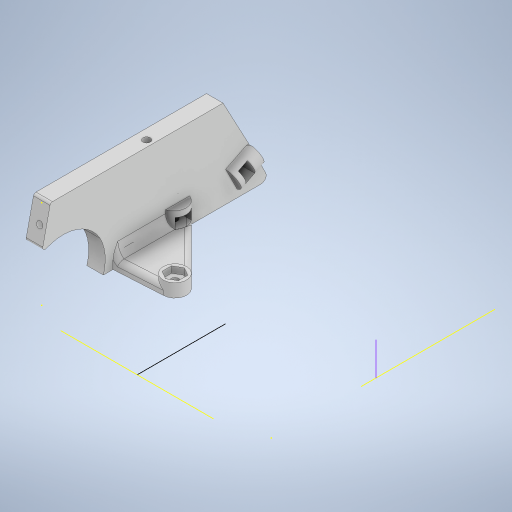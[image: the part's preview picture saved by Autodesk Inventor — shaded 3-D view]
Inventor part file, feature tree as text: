
AUTODESK INVENTOR PART (.ipt)
format: ipt  version: 2023 (Build 270158000, 158)  size: 3,066,368 bytes
history: native  units: mm
features: projected_geometry x135, extrude x121, sketch x89, fillet x11, reference x5, plane x3, mirror x3, other x3
ambient origin geometry x8: Origin, YZ Plane, XZ Plane, XY Plane, X Axis, Y Axis, Z Axis, Center Point
bodies: Solid1 (feature_tree)
feature tree (370):
  sketch  "Sketch1"  dims[d0=100.0mm d1=100.0mm]
  extrude  "Extrusion1"  Depth=100.0mm
  extrude  "Extrusion2"  Depth=20.0mm
  extrude  "Extrusion3"  Depth=20.0mm
  sketch  "Sketch3"  dims[d4=31.0mm d5=20.0mm]
  extrude  "Extrusion4"  Depth=19.0mm
  extrude  "Extrusion5"  Depth=10.0mm
  sketch  "Sketch4"  dims[d6=14.0mm d7=19.0mm]
  plane  "Work Plane1"
  mirror  "Mirror1"
  extrude  "Extrusion6"  Depth=10.0mm
  sketch  "Sketch8"  dims[d10=10.0mm d11=2.0mm]
  extrude  "Extrusion7"  Depth=15.0mm
  extrude  "Extrusion8"  Depth=2.0mm
  extrude  "Extrusion9"  Depth=1.0mm
  sketch  "Sketch9"  dims[d12=2.0mm d13=15.0mm]
  extrude  "Extrusion10"  Depth=10.0mm TaperAngle=0.0deg
  extrude  "Extrusion11"  TaperAngle=0.0deg  [1 undecoded]
  sketch  "Sketch10"  dims[d14=15.0mm d15=2.0mm]
  extrude  "Extrusion12"  Depth=14.0mm TaperAngle=0.0deg
  extrude  "Extrusion13"  TaperAngle=90.0deg  [1 undecoded]
  extrude  "Extrusion14"  Depth=40.0mm
  sketch  "Sketch12"  dims[d18=10.0mm d19=0.0mm d20=2.0mm d21=0.0mm]
  extrude  "Extrusion15"  Depth=25.0mm
  extrude  "Extrusion16"  Depth=5.0mm
  extrude  "Extrusion17"  Depth=13.0mm
  extrude  "Extrusion18"  Depth=8.0mm
  extrude  "Extrusion19"  Depth=18.0mm TaperAngle=0.0deg
  extrude  "Extrusion20"  Depth=49.0mm
  extrude  "Extrusion21"  Depth=5.0mm
  sketch  "Sketch15"  dims[d28=14.25mm d29=0.0mm d30=90.0deg]
  plane  "Work Plane2"
  mirror  "Mirror2"
  extrude  "Extrusion22"  TaperAngle=0.0deg  [1 undecoded]
  sketch  "Sketch17"  dims[d36=15.0mm d37=25.0mm]
  extrude  "Extrusion23"  Depth=10.0mm
  extrude  "Extrusion24"  Depth=1.6mm
  extrude  "Extrusion25"  TaperAngle=0.0deg  [1 undecoded]
  extrude  "Extrusion26"  Depth=14.0mm TaperAngle=0.0deg
  extrude  "Extrusion27"  Depth=6.0mm
  sketch  "Sketch21"  dims[d44=18.0mm d45=0.0mm d46=18.0mm d47=0.0mm]
  extrude  "Extrusion28"  Depth=2.0mm
  extrude  "Extrusion29"  Depth=6.0mm TaperAngle=0.0deg
  sketch  "Sketch22"  dims[d48=0.0mm d49=0.0mm d50=49.0mm]
  extrude  "Extrusion30"  Depth=15.0mm TaperAngle=0.0deg
  extrude  "Extrusion31"  Depth=3.2mm
  extrude  "Extrusion32"  Depth=4.0mm
  extrude  "Extrusion33"  Depth=1.0mm TaperAngle=0.0deg
  extrude  "Extrusion34"  Depth=3.0mm
  extrude  "Extrusion35"  Depth=15.0mm TaperAngle=0.0deg
  extrude  "Extrusion36"  Depth=3.2mm
  fillet  "Face Fillet1"
  fillet  "Face Fillet2"
  extrude  "Extrusion37"  Depth=3.2mm
  fillet  "Face Fillet3"
  fillet  "Face Fillet5"
  extrude  "Extrusion38"  Depth=5.0mm TaperAngle=0.0deg
  extrude  "Extrusion39"  TaperAngle=0.0deg  [1 undecoded]
  fillet  "Fillet2"  Radius=2.8mm
  extrude  "Extrusion40"  Depth=100.0mm TaperAngle=0.0deg
  sketch  "Sketch32"  dims[d76=6.0mm d77=0.0mm d78=15.0mm d79=0.0mm]
  extrude  "Extrusion41"  Depth=11.0mm
  extrude  "Extrusion42"  Depth=9.0mm TaperAngle=0.0deg
  extrude  "Extrusion43"  Depth=3.2mm
  sketch  "Sketch33"  dims[d80=15.0mm d81=0.0mm d82=3.2mm]
  extrude  "Extrusion44"  Depth=7.0mm TaperAngle=0.0deg
  extrude  "Extrusion45"  Depth=40.656mm TaperAngle=0.0deg
  extrude  "Extrusion46"  Depth=9.0mm TaperAngle=0.0deg
  extrude  "Extrusion47"  Depth=3.0mm
  sketch  "Sketch36"  dims[d91=90.0deg d92=3.0mm]
  extrude  "Extrusion48"  Depth=1.5mm TaperAngle=0.0deg
  extrude  "Extrusion49"  Depth=6.0mm
  sketch  "Sketch37"  dims[d93=3.0mm d94=15.0mm d95=0.0mm]
  extrude  "Extrusion50"  Depth=10.0mm TaperAngle=0.0deg
  extrude  "Extrusion51"  Depth=4.0mm
  extrude  "Extrusion52"  Depth=10.0mm TaperAngle=0.0deg
  extrude  "Extrusion53"  Depth=20.0mm TaperAngle=0.0deg
  sketch  "Sketch40"  dims[d100=4.0mm d101=5.0mm d102=0.0mm]
  extrude  "Extrusion54"  Depth=1.5mm
  extrude  "Extrusion55"  Depth=3.0mm
  extrude  "Extrusion56"  Depth=6.4mm
  extrude  "Extrusion57"  Depth=3.0mm
  fillet  "Fillet3"  Radius=2.0mm
  extrude  "Extrusion58"  TaperAngle=0.0deg  [1 undecoded]
  sketch  "Sketch44"  dims[d114=3.4mm d115=9.0mm d116=0.0mm]
  extrude  "Extrusion59"  TaperAngle=0.0deg  [1 undecoded]
  extrude  "Extrusion60"  Depth=10.0mm TaperAngle=0.0deg
  sketch  "Sketch45"  dims[d117=15.0mm d118=0.0mm d119=3.2mm]
  extrude  "Extrusion61"  Depth=10.0mm TaperAngle=0.0deg
  extrude  "Extrusion62"  Depth=3.0mm
  sketch  "Sketch46"  dims[d120=3.2mm d121=7.0mm d122=0.0mm]
  extrude  "Extrusion63"  Depth=6.5mm TaperAngle=0.0deg
  extrude  "Extrusion64"  Depth=17.0mm TaperAngle=0.0deg
  extrude  "Extrusion65"  Depth=3.0mm
  extrude  "Extrusion66"  Depth=5.0mm TaperAngle=0.0deg
  sketch  "Sketch49"  dims[d138=28.734mm d139=3.0mm]
  extrude  "Extrusion67"  Depth=6.5mm TaperAngle=0.0deg
  extrude  "Extrusion68"  Depth=14.0mm TaperAngle=0.0deg
  extrude  "Extrusion69"  Depth=6.5mm
  extrude  "Extrusion70"  Depth=6.5mm TaperAngle=0.0deg
  extrude  "Extrusion71"  Depth=17.0mm TaperAngle=0.0deg
  extrude  "Extrusion72"  Depth=2.5mm
  extrude  "Extrusion73"  Depth=2.0mm
  extrude  "Extrusion74"  TaperAngle=0.0deg  [1 undecoded]
  extrude  "Extrusion75"  Depth=6.5mm TaperAngle=0.0deg
  extrude  "Extrusion76"  Depth=1.0mm
  sketch  "Sketch53"  dims[d149=6.7mm d152=4.0mm]
  extrude  "Extrusion77"  Depth=1.0mm
  extrude  "Extrusion78"  Depth=3.0mm
  extrude  "Extrusion79"  Depth=15.0mm TaperAngle=0.0deg
  extrude  "Extrusion80"  Depth=10.0mm TaperAngle=0.0deg
  extrude  "Extrusion81"  Depth=10.0mm TaperAngle=0.0deg
  extrude  "Extrusion82"  Depth=4.0mm TaperAngle=0.0deg
  extrude  "Extrusion83"  Depth=10.0mm TaperAngle=0.0deg
  sketch  "Sketch59"  dims[d166=6.4mm d167=3.0mm d169=2.0mm]
  extrude  "Extrusion84"  Depth=7.0mm
  extrude  "Extrusion85"  Depth=6.5mm TaperAngle=0.0deg
  extrude  "Extrusion86"  Depth=4.0mm TaperAngle=0.0deg
  extrude  "Extrusion87"  Depth=1.0mm
  extrude  "Extrusion88"  Depth=10.0mm TaperAngle=0.0deg
  sketch  "Sketch62"  dims[d178=10.0mm d179=0.0mm d180=4.0mm d181=0.0mm]
  extrude  "Extrusion89"  Depth=10.0mm
  extrude  "Extrusion90"  Depth=10.0mm
  fillet  "Fillet4"  Radius=30.0mm
  extrude  "Extrusion91"  Depth=10.0mm
  extrude  "Extrusion92"  Depth=10.0mm
  extrude  "Extrusion93"  Depth=10.0mm TaperAngle=0.0deg
  extrude  "Extrusion94"  TaperAngle=135.0deg  [1 undecoded]
  extrude  "Extrusion95"  TaperAngle=0.0deg  [1 undecoded]
  sketch  "Sketch68"  dims[d205=4.0mm d206=0.0mm d207=5.0mm d208=0.0mm]
  extrude  "Extrusion96"  Depth=10.0mm TaperAngle=0.0deg
  extrude  "Extrusion97"  Depth=10.0mm
  extrude  "Extrusion98"  Depth=10.0mm
  extrude  "Extrusion99"  Depth=10.0mm
  extrude  "Extrusion100"  TaperAngle=0.0deg  [1 undecoded]
  sketch  "Sketch74"  dims[d219=6.5mm d220=0.0mm d221=16.0mm d222=0.0mm]
  extrude  "Extrusion101"  Depth=1.0mm TaperAngle=0.0deg
  extrude  "Extrusion102"  Depth=10.0mm TaperAngle=0.0deg
  extrude  "Extrusion103"  Depth=10.0mm TaperAngle=0.0deg
  extrude  "Extrusion104"  Depth=10.0mm TaperAngle=0.0deg
  extrude  "Extrusion105"  Depth=10.0mm TaperAngle=0.0deg
  fillet  "Fillet6"  Radius=12.0mm
  fillet  "Fillet7"  Radius=2.0mm
  extrude  "Extrusion106"  Depth=10.0mm TaperAngle=0.0deg
  fillet  "Fillet8"  Radius=5.0mm
  extrude  "Extrusion107"  Depth=6.5mm TaperAngle=0.0deg
  sketch  "Sketch80"  dims[d239=1.0mm d240=2.5mm]
  extrude  "Extrusion108"  Depth=10.0mm
  extrude  "Extrusion109"  Depth=10.0mm TaperAngle=0.0deg
  extrude  "Extrusion110"  Depth=10.0mm TaperAngle=0.0deg
  extrude  "Extrusion111"  Depth=10.0mm
  extrude  "Extrusion112"  Depth=10.0mm
  fillet  "Fillet9"  Radius=3.5mm
  extrude  "Extrusion113"  Depth=10.0mm
  extrude  "Extrusion114"  Depth=6.5mm TaperAngle=0.0deg
  extrude  "Extrusion115"  Depth=6.5mm TaperAngle=0.0deg
  plane  "Work Plane3"
  mirror  "Mirror3"
  extrude  "Extrusion116"  Depth=10.0mm
  extrude  "Extrusion117"  Depth=10.0mm TaperAngle=0.0deg
  sketch  "Sketch89"  dims[d269=6.5mm d270=0.0mm d271=3.0mm d272=0.0mm]
  extrude  "Extrusion118"  Depth=10.0mm TaperAngle=0.0deg
  extrude  "Extrusion119"  Depth=10.0mm
  extrude  "Wyciągnięcie proste120"  TaperAngle=90.0deg  [1 undecoded]
  extrude  "Wyciągnięcie proste121"  Depth=10.0mm
  sketch  "Sketch2"  dims[d2=5.0mm d3=20.0mm]
  projected_geometry  "Projected Loop1"
  sketch  "Sketch6"  dims[d8=10.0mm d9=14.0mm]
  projected_geometry  "Projected Loop5"
  projected_geometry  "Projected Loop6"
  projected_geometry  "Projected Loop7"
  projected_geometry  "Projected Loop8"
  projected_geometry  "Projected Loop9"
  projected_geometry  "Projected Loop10"
  sketch  "Sketch11"  dims[d16=1.0mm d17=5.0mm]
  projected_geometry  "Projected Loop11"
  projected_geometry  "Projected Loop12"
  sketch  "Sketch13"  dims[d22=31.0mm d23=0.0mm d24=0.0mm]
  projected_geometry  "Projected Loop13"
  projected_geometry  "Projected Loop14"
  sketch  "Sketch14"  dims[d25=30.4mm d26=14.0mm d27=0.0mm]
  projected_geometry  "Projected Loop15"
  projected_geometry  "Projected Loop16"
  sketch  "Sketch16"  dims[d33=25.0mm d34=0.0mm d35=40.0mm]
  projected_geometry  "Projected Loop17"
  projected_geometry  "Projected Loop18"
  projected_geometry  "Projected Loop19"
  sketch  "Sketch18"  dims[d38=20.0mm d39=5.0mm]
  projected_geometry  "Projected Loop20"
  projected_geometry  "Projected Loop21"
  projected_geometry  "Projected Loop22"
  projected_geometry  "Projected Loop23"
  projected_geometry  "Projected Loop24"
  projected_geometry  "Projected Loop25"
  projected_geometry  "Projected Loop26"
  sketch  "Sketch19"  dims[d40=7.0mm d41=13.0mm]
  projected_geometry  "Projected Loop27"
  sketch  "Sketch20"  dims[d42=7.0mm d43=8.0mm]
  projected_geometry  "Projected Loop28"
  projected_geometry  "Projected Loop29"
  projected_geometry  "Projected Loop30"
  sketch  "Sketch23"  dims[d51=25.0mm d52=5.0mm]
  sketch  "Sketch24"  dims[d53=20.0mm d54=0.0mm d55=0.0mm]
  projected_geometry  "Projected Loop31"
  projected_geometry  "Projected Loop32"
  sketch  "Sketch25"  dims[d56=10.0mm d57=0.0mm d58=1.6mm]
  projected_geometry  "Projected Loop33"
  sketch  "Sketch26"  dims[d59=1.6mm d60=1.6mm]
  projected_geometry  "Projected Loop34"
  sketch  "Sketch27"  dims[d61=5.0mm d62=0.0mm d63=0.0mm d64=0.0mm]
  projected_geometry  "Projected Loop35"
  sketch  "Sketch28"  dims[d65=2.5mm d66=14.0mm d67=0.0mm]
  projected_geometry  "Projected Loop36"
  sketch  "Sketch29"  dims[d68=2.0mm d69=6.0mm]
  sketch  "Sketch30"  dims[d70=5.0mm d71=2.0mm]
  projected_geometry  "Projected Loop37"
  projected_geometry  "Projected Loop38"
  projected_geometry  "Projected Loop39"
  sketch  "Sketch31"  dims[d72=14.0mm d73=0.0mm d74=6.0mm d75=0.0mm]
  projected_geometry  "Projected Loop40"
  projected_geometry  "Projected Loop41"
  projected_geometry  "Projected Loop42"
  projected_geometry  "Projected Loop43"
  projected_geometry  "Projected Loop44"
  projected_geometry  "Projected Loop45"
  projected_geometry  "Projected Loop46"
  sketch  "Sketch34"  dims[d83=3.2mm d84=4.0mm]
  projected_geometry  "Projected Loop47"
  projected_geometry  "Projected Loop48"
  sketch  "Sketch35"  dims[d85=15.0mm d86=0.0mm d87=1.0mm d88=0.0mm]
  projected_geometry  "Projected Loop49"
  projected_geometry  "Projected Loop50"
  projected_geometry  "Projected Loop51"
  projected_geometry  "Projected Loop52"
  projected_geometry  "Projected Loop53"
  sketch  "Sketch38"  dims[d96=3.2mm d97=3.2mm]
  projected_geometry  "Projected Loop54"
  projected_geometry  "Projected Loop55"
  sketch  "Sketch39"  dims[d98=3.2mm d99=3.2mm]
  projected_geometry  "Projected Loop56"
  sketch  "Sketch41"  dims[d103=5.0mm d104=0.0mm d105=0.0mm d106=0.0mm d107=2.8mm]
  projected_geometry  "Projected Loop57"
  sketch  "Sketch42"  dims[d108=2.8mm d109=100.0mm d110=0.0mm]
  projected_geometry  "Projected Loop58"
  sketch  "Sketch43"  dims[d111=20.0mm d112=0.0mm d113=11.0mm]
  projected_geometry  "Projected Loop59"
  projected_geometry  "Projected Loop60"
  projected_geometry  "Projected Loop61"
  projected_geometry  "Projected Loop62"
  projected_geometry  "Projected Loop63"
  projected_geometry  "Projected Loop64"
  projected_geometry  "Projected Loop65"
  projected_geometry  "Projected Loop66"
  projected_geometry  "Projected Loop67"
  projected_geometry  "Projected Loop68"
  projected_geometry  "Projected Loop69"
  projected_geometry  "Projected Loop70"
  projected_geometry  "Projected Loop71"
  projected_geometry  "Projected Loop72"
  projected_geometry  "Projected Loop73"
  projected_geometry  "Projected Loop74"
  projected_geometry  "Projected Loop75"
  projected_geometry  "Projected Loop76"
  projected_geometry  "Projected Loop77"
  projected_geometry  "Projected Loop78"
  sketch  "Sketch47"  dims[d123=4.0mm d124=0.0mm d125=40.656mm d126=0.0mm]
  projected_geometry  "Projected Loop79"
  sketch  "Sketch48"  dims[d127=3.0mm d128=0.0mm d129=9.0mm d130=0.0mm]
  projected_geometry  "Projected Loop80"
  projected_geometry  "Projected Loop81"
  sketch  "Sketch50"  dims[d140=1.5mm d141=0.0mm d142=1.5mm d143=0.0mm]
  projected_geometry  "Projected Loop82"
  projected_geometry  "Projected Loop83"
  sketch  "Sketch51"  dims[d144=6.0mm d145=6.0mm]
  projected_geometry  "Projected Loop84"
  sketch  "Sketch52"  dims[d146=2.0mm d147=10.0mm d148=0.0mm]
  projected_geometry  "Projected Loop85"
  projected_geometry  "Projected Loop86"
  projected_geometry  "Projected Loop87"
  sketch  "Sketch54"  dims[d153=10.0mm d154=0.0mm d155=16.0mm d156=0.0mm]
  projected_geometry  "Projected Loop88"
  projected_geometry  "Projected Loop89"
  sketch  "Sketch55"  dims[d157=1e-05mm d158=20.0mm d159=0.0mm]
  projected_geometry  "Projected Loop90"
  projected_geometry  "Projected Loop91"
  sketch  "Sketch56"  dims[d160=6.4mm d161=1.5mm]
  projected_geometry  "Projected Loop92"
  projected_geometry  "Projected Loop93"
  projected_geometry  "Projected Loop94"
  sketch  "Sketch57"  dims[d162=16.5mm d163=3.0mm]
  projected_geometry  "Projected Loop95"
  projected_geometry  "Projected Loop96"
  projected_geometry  "Projected Loop97"
  sketch  "Sketch58"  dims[d164=3.0mm d165=6.4mm]
  projected_geometry  "Projected Loop98"
  projected_geometry  "Projected Loop99"
  projected_geometry  "Projected Loop100"
  projected_geometry  "Projected Loop101"
  sketch  "Sketch60"  dims[d170=5.928mm d171=0.0mm d172=0.0mm d173=0.0mm]
  projected_geometry  "Projected Loop102"
  projected_geometry  "Projected Loop103"
  sketch  "Sketch61"  dims[d174=3.0mm d175=0.0mm d176=0.0mm d177=0.0mm]
  projected_geometry  "Projected Loop104"
  projected_geometry  "Projected Loop105"
  projected_geometry  "Projected Loop106"
  projected_geometry  "Projected Loop107"
  projected_geometry  "Projected Loop108"
  projected_geometry  "Projected Loop109"
  projected_geometry  "Projected Loop110"
  projected_geometry  "Projected Loop111"
  sketch  "Sketch63"  dims[d182=2.5mm d183=10.0mm d184=0.0mm]
  projected_geometry  "Projected Loop112"
  sketch  "Sketch64"  dims[d185=2.0mm d186=3.0mm]
  projected_geometry  "Projected Loop113"
  sketch  "Sketch65"  dims[d195=0.0mm d196=0.0mm d197=6.5mm d198=0.0mm]
  projected_geometry  "Projected Loop114"
  reference  "Reference1"
  sketch  "Sketch66"  dims[d199=2.5mm d200=17.0mm d201=0.0mm]
  reference  "Reference2"
  reference  "Reference3"
  sketch  "Sketch67"  dims[d202=14.0mm d203=0.0mm d204=3.0mm]
  projected_geometry  "Projected Loop115"
  projected_geometry  "Projected Loop116"
  sketch  "Sketch69"  dims[d209=2.5mm d210=6.5mm d211=0.0mm]
  projected_geometry  "Projected Loop117"
  sketch  "Sketch72"  dims[d212=0.0mm d213=0.0mm d214=14.0mm d215=0.0mm]
  projected_geometry  "Projected Loop118"
  sketch  "Sketch73"  dims[d216=6.5mm d217=0.0mm d218=2.0mm]
  projected_geometry  "Projected Loop119"
  projected_geometry  "Projected Loop120"
  sketch  "Sketch75"  dims[d223=17.0mm d224=0.0mm d225=17.0mm d226=0.0mm]
  reference  "Reference4"
  projected_geometry  "Projected Loop121"
  sketch  "Sketch76"  dims[d227=17.0mm d228=0.0mm d229=2.5mm]
  projected_geometry  "Projected Loop122"
  sketch  "Sketch77"  dims[d230=2.5mm d231=2.0mm]
  projected_geometry  "Projected Loop123"
  sketch  "Sketch78"  dims[d232=13.0mm d233=0.0mm d234=0.0mm]
  projected_geometry  "Projected Loop124"
  sketch  "Sketch79"  dims[d235=6.5mm d236=0.0mm d237=3.0mm d238=0.0mm]
  projected_geometry  "Projected Loop125"
  projected_geometry  "Projected Loop126"
  projected_geometry  "Projected Loop127"
  sketch  "Sketch81"  dims[d241=14.0mm d242=0.0mm d243=1.0mm]
  sketch  "Sketch82"  dims[d244=2.0mm d245=3.0mm]
  projected_geometry  "Projected Loop128"
  sketch  "Sketch83"  dims[d246=3.2mm d247=15.0mm d248=0.0mm]
  projected_geometry  "Projected Loop129"
  projected_geometry  "Projected Loop130"
  sketch  "Sketch84"  dims[d249=10.0mm d250=0.0mm d251=10.0mm d252=0.0mm]
  projected_geometry  "Projected Loop131"
  reference  "Reference5"
  projected_geometry  "Projected Loop132"
  sketch  "Sketch85"  dims[d253=3.0mm d254=0.0mm d255=10.0mm d256=0.0mm]
  sketch  "Sketch86"  dims[d257=8.0mm d258=0.0mm d259=4.0mm d260=0.0mm]
  sketch  "Sketch87"  dims[d261=2.5mm d262=10.0mm d263=0.0mm]
  projected_geometry  "Projected Loop133"
  projected_geometry  "Projected Loop134"
  sketch  "Sketch88"  dims[d266=7.0mm d268=7.0mm]
  projected_geometry  "Projected Loop135"
  sketch  "Sketch90"  dims[d273=8.0mm d274=0.0mm d275=4.0mm d276=0.0mm]
  sketch  "Sketch91"  dims[d277=1.0mm d278=1.0mm d279=10.0mm d280=0.0mm d281=1.308997mm d282=45.0mm d283=30.0mm d284=0.0mm d285=2.0mm d286=2.5mm d287=11.0mm d288=0.0mm d289=135.0deg d290=0.0mm d291=0.0mm d292=3.7mm d293=0.0mm d294=10.0mm d295=6.4mm d296=3.0mm d297=0.0mm d298=0.0mm d299=1.0mm d300=0.0mm d301=1.5mm d302=0.0mm d303=5.928mm d304=0.0mm d305=12.0mm d306=0.0mm d307=12.0mm d308=0.0mm d309=12.0mm d310=0.0mm d311=2.0mm d312=41.5mm d313=0.0mm d314=5.0mm d315=0.0mm d316=6.5mm d317=0.0mm d318=2.5mm d319=15.0mm d320=0.0mm d321=15.0mm d322=0.0mm d323=6.4mm d324=1.5mm d325=3.5mm d326=3.5mm d327=6.5mm d328=0.0mm d329=6.5mm d330=0.0mm d331=1.047198mm d332=11.908mm d333=0.0mm d334=12.0mm d335=0.0mm d336=8.0mm d337=90.0deg d338=2.7mm d339=10.0mm d340=0.0mm d341=6.4mm d342=10.0mm d343=0.0mm d344=6.5mm d345=0.0mm d346=6.5mm d347=0.0mm d348=6.5mm d349=0.0mm d350=6.5mm d351=0.0mm d353=1.0mm d354=1.0mm d355=6.5mm d356=0.0mm d357=1.0mm d358=2.0mm d359=6.5mm d360=0.0mm d361=4.0mm d362=0.0mm d363=4.0mm d364=0.0mm d365=44.0mm d366=0.0mm d367=6.5mm d368=0.0mm d369=6.5mm d370=0.0mm d371=1.0mm d372=4.0mm d373=10.0mm d374=0.0mm d375=15.0mm d376=0.0mm d377=12.0mm d378=0.0mm d379=41.75mm d380=6.0mm d381=6.0mm d382=6.5mm d383=0.0mm d384=4.0mm d385=0.0mm d386=0.0mm d387=0.0mm d388=1.5mm d389=1.5mm d390=10.0mm d391=0.0mm d392=10.0mm d393=0.0mm d394=10.0mm d395=0.0mm d150=0.0mm d151=0.0mm d352=0.0mm]
  projected_geometry  "Projected Loop136"
  sketch  "Szkic92"
  projected_geometry  "Pętla rzutowana137"
  sketch  "Szkic93"
  projected_geometry  "Pętla rzutowana138"
  parser-record x1  (decoder bookkeeping rows leaked as tree rows — omitted from the tree; the rows remain in map.json)
  other  "zlozenie.iam"
  other  "sciana_lewa_v4:1"
note: 12 required parameter values undecoded (feature->parameter linkage not recoverable at this tier; creation-order binding heuristic only, values carry confidence <= 0.55)
note: 1 file-system path scrubbed to <path> (originals preserved in map.json)
